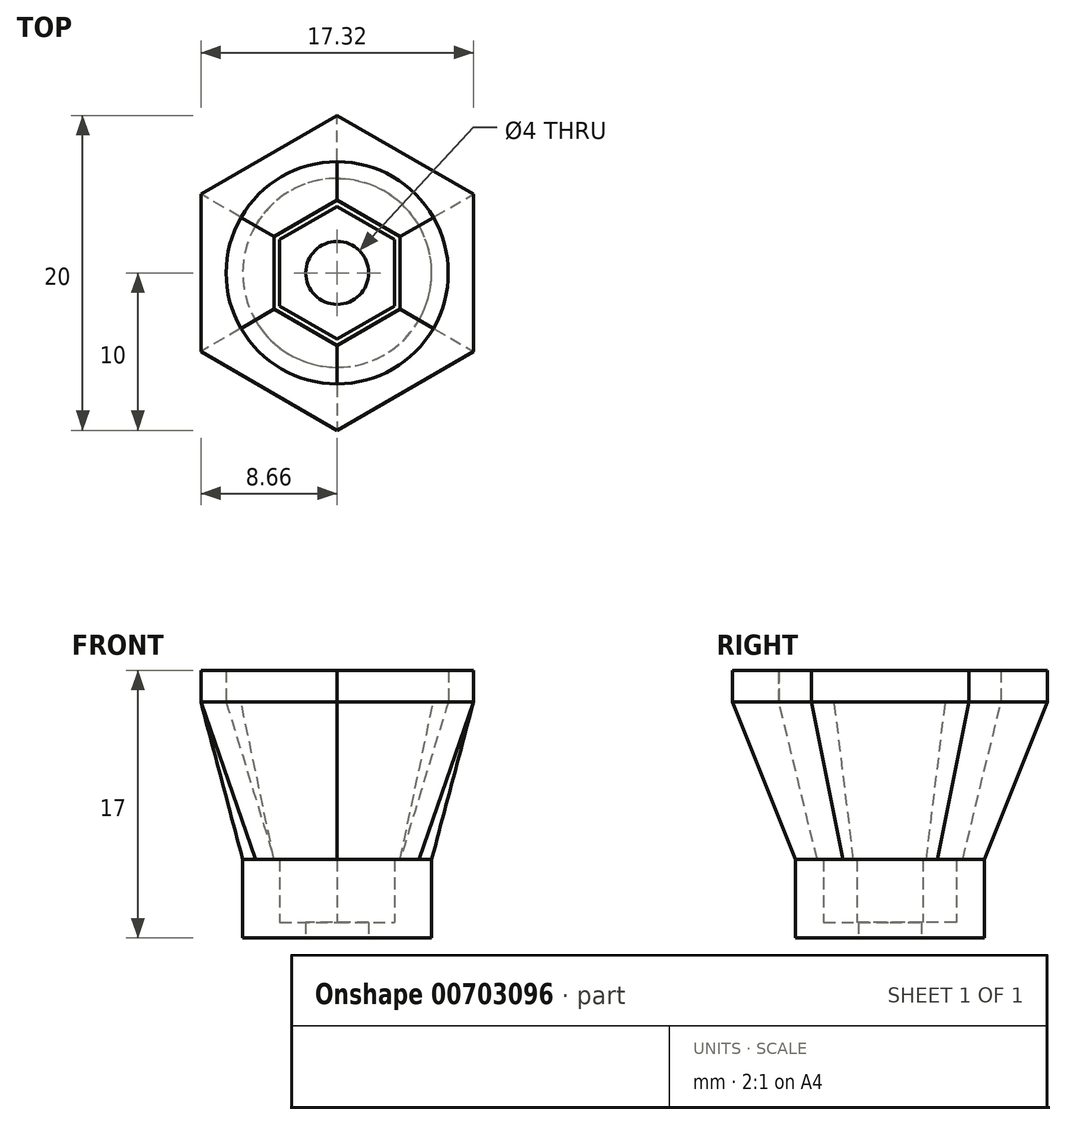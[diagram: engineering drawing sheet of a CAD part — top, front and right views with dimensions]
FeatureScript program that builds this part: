
annotation { "Feature Type Name" : "Feature", "Feature Type Description" : "" }
export const myFeature = defineFeature(function(context is Context, id is Id, definition is map)
    precondition{}
    {
        {
            var Q0;
            Q0=qCreatedBy(makeId("Top.planeOp"),FACE);
            var sketch = newSketch(context, id + "F0", { "sketchPlane" : qUnion([Q0])});
            skCircle(sketch, "E0", {"center": v(0, 0) * mm, "radius": 2 * mm});
            skCircle(sketch, "E1.cCircle", {"center": v(0, 0) * mm, "radius": 3.65 * mm, "construction": true});
            skLineSegment(sketch, "E1.0", {"start": v(3.65, 2.1) * mm, "end": v(3.65, -2.1) * mm});
            skLineSegment(sketch, "E1.1", {"start": v(3.65, -2.1) * mm, "end": v(0, -4.21) * mm});
            skLineSegment(sketch, "E1.2", {"start": v(0, -4.21) * mm, "end": v(-3.65, -2.1) * mm});
            skLineSegment(sketch, "E1.3", {"start": v(-3.65, -2.1) * mm, "end": v(-3.65, 2.1) * mm});
            skLineSegment(sketch, "E1.4", {"start": v(-3.65, 2.1) * mm, "end": v(0, 4.21) * mm});
            skLineSegment(sketch, "E1.5", {"start": v(0, 4.21) * mm, "end": v(3.65, 2.1) * mm});
            skPoint(sketch, "E1.0.midPoint", {"position": v(3.65, 0) * mm});
            skCircle(sketch, "E2", {"center": v(0, 0) * mm, "radius": 6 * mm});
            skSolve(sketch);
        }
        {
            var Q0;
            Q0=makeQuery(id+"F0.imprint","IMPRINT",FACE,{"disambiguationData":[TD([[makeQuery(id+"F0.imprint","IMPRINT",EDGE,{"derivedFrom":sQuery(id+"F0.wireOp",EDGE,"E1.0")}),1.0]])]});
            var Q1;
            Q1=makeQuery(id+"F0.imprint","IMPRINT",FACE,{"disambiguationData":[TD([[makeQuery(id+"F0.imprint","IMPRINT",EDGE,{"derivedFrom":sQuery(id+"F0.wireOp",EDGE,"E0")}),-1.0]])]});
            extrude(context, id + "F1", {"entities" : qUnion([Q0, Q1]), "depth" : 5 * mm, "offsetDistance" : 25 * mm});
        }
        {
            var Q0;
            Q0=makeQuery(id+"F0.imprint","IMPRINT",FACE,{"disambiguationData":[TD([[makeQuery(id+"F0.imprint","IMPRINT",EDGE,{"derivedFrom":sQuery(id+"F0.wireOp",EDGE,"E0")}),-1.0]])]});
            extrude(context, id + "F2", {"entities" : qUnion([Q0]), "operationType" : NewBodyOperationType.REMOVE, "depth" : 25 * mm, "offsetDistance" : 25 * mm, "hasSecondDirection" : true, "secondDirectionOppositeDirection" : false, "secondDirectionDepth" : 1 * mm});
        }
        {
            var Q0;
            Q0=qCreatedBy(makeId("Top.planeOp"),FACE);
            cPlane(context, id + "F3", {"entities" : qUnion([Q0]), "cplaneType" : CPlaneType.OFFSET, "offset" : 15 * mm, "width" : 150 * mm, "height" : 150 * mm});
        }
        {
            var Q0;
            Q0=makeQuery(id+"F1.opExtrude","CAP_FACE",FACE,{"disambiguationData":[OSD([sQuery(id+"F0.wireOp",EDGE,"E0"),sQuery(id+"F0.wireOp",EDGE,"E2")])],"isStart":false});
            cPlane(context, id + "F4", {"entities" : qUnion([Q0]), "cplaneType" : CPlaneType.OFFSET, "offset" : 0 * mm, "width" : 150 * mm, "height" : 150 * mm});
        }
        {
            var Q0;
            Q0=qCreatedBy(id+"F4.planeOp",FACE);
            var sketch = newSketch(context, id + "F5", { "sketchPlane" : qUnion([Q0])});
            skCircle(sketch, "E3", {"center": v(0, 0) * mm, "radius": 6 * mm});
            skSolve(sketch);
        }
        {
            var Q0;
            Q0=qCreatedBy(id+"F3.planeOp",FACE);
            var sketch = newSketch(context, id + "F6", { "sketchPlane" : qUnion([Q0])});
            skCircle(sketch, "E4.cCircle", {"center": v(0, 0) * mm, "radius": 8.66 * mm, "construction": true});
            skLineSegment(sketch, "E4.0", {"start": v(8.66, 5) * mm, "end": v(8.66, -5) * mm});
            skLineSegment(sketch, "E4.1", {"start": v(8.66, -5) * mm, "end": v(0, -10) * mm});
            skLineSegment(sketch, "E4.2", {"start": v(0, -10) * mm, "end": v(-8.66, -5) * mm});
            skLineSegment(sketch, "E4.3", {"start": v(-8.66, -5) * mm, "end": v(-8.66, 5) * mm});
            skLineSegment(sketch, "E4.4", {"start": v(-8.66, 5) * mm, "end": v(0, 10) * mm});
            skLineSegment(sketch, "E4.5", {"start": v(0, 10) * mm, "end": v(8.66, 5) * mm});
            skPoint(sketch, "E4.0.midPoint", {"position": v(8.66, 0) * mm});
            skSolve(sketch);
        }
        {
            var Q1;
            Q1 = qSketchRegion(id + "F5", true);
            var Q2;
            Q2 = qSketchRegion(id + "F6", true);
            loft(context, id + "F7", {"operationType" : NewBodyOperationType.ADD, "sheetProfilesArray" : [{ "sheetProfileEntities" : qUnion([Q1]) }, { "sheetProfileEntities" : qUnion([Q2]) }]});
        }
        {
            var Q0;
            Q0=qCreatedBy(id+"F4.planeOp",FACE);
            var sketch = newSketch(context, id + "F8", { "sketchPlane" : qUnion([Q0])});
            skCircle(sketch, "E5.cCircle", {"center": v(0, 0) * mm, "radius": 4 * mm, "construction": true});
            skLineSegment(sketch, "E5.0", {"start": v(4, 2.3) * mm, "end": v(4, -2.3) * mm});
            skLineSegment(sketch, "E5.1", {"start": v(4, -2.3) * mm, "end": v(0, -4.62) * mm});
            skLineSegment(sketch, "E5.2", {"start": v(0, -4.62) * mm, "end": v(-4, -2.3) * mm});
            skLineSegment(sketch, "E5.3", {"start": v(-4, -2.3) * mm, "end": v(-4, 2.3) * mm});
            skLineSegment(sketch, "E5.4", {"start": v(-4, 2.3) * mm, "end": v(0, 4.62) * mm});
            skLineSegment(sketch, "E5.5", {"start": v(0, 4.62) * mm, "end": v(4, 2.3) * mm});
            skPoint(sketch, "E5.0.midPoint", {"position": v(4, 0) * mm});
            skSolve(sketch);
        }
        {
            var Q0;
            Q0=qCreatedBy(id+"F3.planeOp",FACE);
            var sketch = newSketch(context, id + "F9", { "sketchPlane" : qUnion([Q0])});
            skCircle(sketch, "E6", {"center": v(0, 0) * mm, "radius": 7.06 * mm});
            skSolve(sketch);
        }
        {
            var Q1;
            Q1 = qSketchRegion(id + "F8", true);
            var Q2;
            Q2 = qSketchRegion(id + "F9", true);
            loft(context, id + "F10", {"operationType" : NewBodyOperationType.REMOVE, "sheetProfilesArray" : [{ "sheetProfileEntities" : qUnion([Q1]) }, { "sheetProfileEntities" : qUnion([Q2]) }]});
        }
        {
            var Q0;
            Q0=makeQuery(id+"F7.opLoft","CAP_FACE",FACE,{"disambiguationData":[OSD([makeQuery(id+"F6.imprint","IMPRINT",FACE,{"disambiguationData":[TD([[makeQuery(id+"F6.imprint","IMPRINT",EDGE,{"derivedFrom":sQuery(id+"F6.wireOp",EDGE,"E4.0")}),-1.0]])]})])],"isStart":true});
            extrude(context, id + "F11", {"entities" : qUnion([Q0]), "operationType" : NewBodyOperationType.ADD, "depth" : 2 * mm, "offsetDistance" : 25 * mm});
        }
    });
